# Revit family: Haworth_Cappellini_WandersTulip_Chair_AP_PRELIMINARY
name_source: partatom
category: Furniture
units: mm (PartAtom-declared; Revit-internal decimal feet)

## family parameters
Always vertical = Yes
Cut with Voids When Loaded = No
OmniClass Number = 23.40.20.00
OmniClass Title = General Furniture and Specialties
Room Calculation Point = No
Shared = No
Work Plane-Based = No

## types (1)
- Wanders Tulip
    Actual Depth = 870 mm  [stored 2.85433 ft]
    Actual Height = 1630 mm  [stored 5.34777 ft]
    Actual Width = 870 mm  [stored 2.85433 ft]
    Assembly Code = E2020200
    Description = Haworth - Cappellini - Wanders Tulip Chair
    Manufacturer = Haworth
    Model = TL_1
    Revision Number = 1
    Size = Verify Final Dim. w/ Haworth
    URL = https://www.haworth.com
    URL - Product = https://www.haworth.com
    Warranty = http://www.haworth.com

note: [stored X ft] marks values corroborated as IEEE doubles in the binary element streams (Revit-internal decimal feet)

## geometry (parser evidence)
native form markers: Sweep x2
no freeform markers — native parametric forms only
